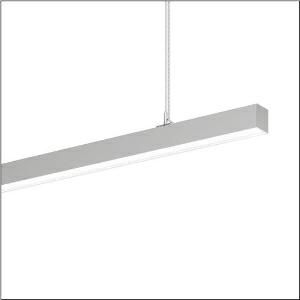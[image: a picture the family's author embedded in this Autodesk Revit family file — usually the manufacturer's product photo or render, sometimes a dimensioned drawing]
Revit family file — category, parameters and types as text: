
# Revit family: silica_r__21_51mx33db49sb_c15f
name_source: partatom
category: Lighting Fixtures
units: mm (PartAtom-declared; Revit-internal decimal feet)

## family parameters
Cut with Voids When Loaded = No
Host = Face
Light Source = No
Part Type = Normal
Room Calculation Point = No
Round Connector Dimension = Use Diameter
Shared = No

## types (1)
- --- (1 x LED, 7390 lm, 48.3 W, 4000K)
    Apparent Load = 48 VA
    CIE Flux Codes = 78 96 99 55 100
    Color Rendering = 80
    Color Temperature = 4000K
    Default Elevation = 1800 mm
    Description = Silica® 21, office luminaire, primary optical cover: prismatic diffuser, of PMMA, CAT 2 (L<= 3000cd/m²), light emission: direct/indirect distribution, primary light characteristic: symmetric, installation type: suspended mounting, LED, rated luminous flux: 7.390lm, luminous efficacy: 153lm/W, light colour: 840, colour temperature: 4000K, with terminal, 3+2-pole, max. 2.5mm², mains connection: 220..240V, AC, 50/60Hz, rated input power: 48.3W, luminaire housing, of aluminium, metallic grey (RAL 9006), length: 1.504mm, width: 53mm, height: 53mm, protection rating (complete): IP20, insulation class (complete): insulation class I (protective earthing), certification: CE, permissible operating ambient temperature: 0..+35°C, standard: EN 50419, packaging unit: 1 piece
    Height = 53 mm
    Lamp = 1 x LED
    Lamp Light Flux = 7390 lm
    Lamp Power = 48.3 W
    Lamp count = 1
    Length = 1504 mm
    Luminous efficacy = 153 lm/W
    Manufacturer = Siteco
    ModVariant = No
    Model = 51MX33DB49SB
    Mounting Place = Ceiling
    Mounting Type = Pendant
    Number of Poles = 1
    OnlyDefault = Yes
    Power Factor = 1
    Product Name = Silica® 21
    Product group = office luminaire | ceiling pendant
    ProductGroupID = 902
    Protection Class = Protection class I
    Protection Degree = IP 20
    RLX_Detail_Level = 1
    RLX_Emergency_Light_Flux = 0 lm
    RLX_Emergency_Type = 0
    RLX_Emergency_Type_DB = No
    RlxData = <blob elided: 23565 chars, md5=c3da0cb8>
    Socket = socket
    Standby Power = 0 W
    System Light Flux = 7390 lm
    System Power = 48 W
    Type Comments = factory setting: luminous flux: 100 % | dim-lin: 254 | 323 mA
    Type Image = l_1335864.jpg
    URL = http://relux.com
    VarID = @adj_087503
    Voltage = 0 V
    Weight = 0.00 kg
    Width = 53 mm

## geometry (parser evidence)
native form markers: Blend x4, Sweep x14
no freeform markers — native parametric forms only
